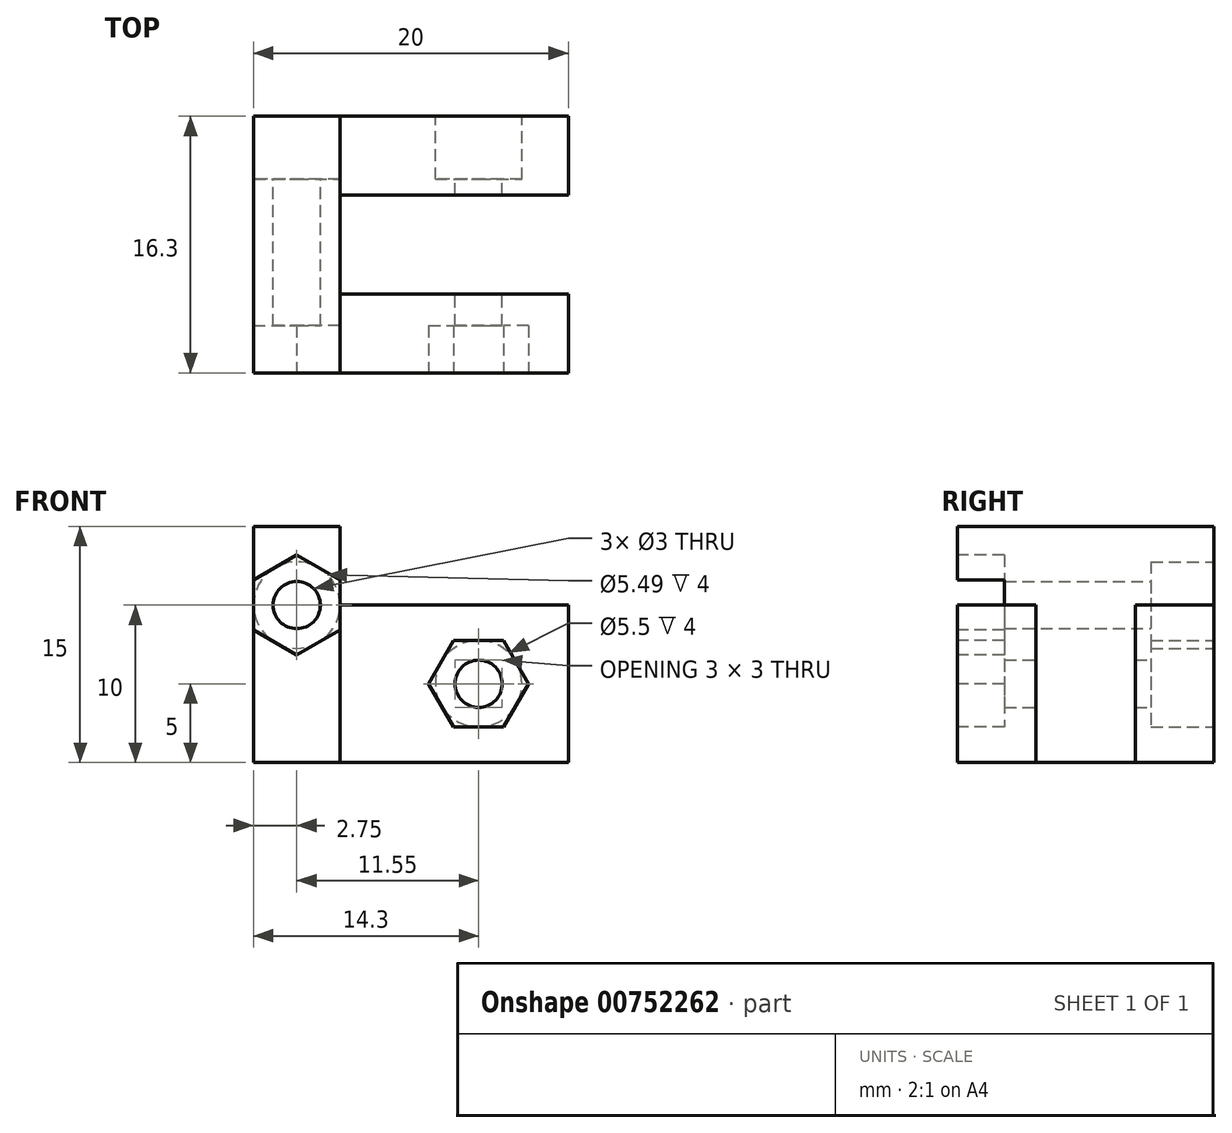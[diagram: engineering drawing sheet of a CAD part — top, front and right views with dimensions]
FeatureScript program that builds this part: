
annotation { "Feature Type Name" : "Feature", "Feature Type Description" : "" }
export const myFeature = defineFeature(function(context is Context, id is Id, definition is map)
    precondition{}
    {
        {
            var Q0;
            Q0=qCreatedBy(makeId("Top.planeOp"),FACE);
            var sketch = newSketch(context, id + "F0", { "sketchPlane" : qUnion([Q0])});
            skLineSegment(sketch, "E0", {"start": v(0, -3.15) * mm, "end": v(-14.5, -3.15) * mm});
            skLineSegment(sketch, "E1", {"start": v(0, -3.15) * mm, "end": v(0, -8.15) * mm});
            skLineSegment(sketch, "E2", {"start": v(0, -8.15) * mm, "end": v(-14.5, -8.15) * mm});
            skLineSegment(sketch, "E3", {"start": v(-14.5, -8.15) * mm, "end": v(-20, -8.15) * mm});
            skLineSegment(sketch, "E4", {"start": v(-20, -8.15) * mm, "end": v(-20, 0) * mm});
            skLineSegment(sketch, "E5", {"start": v(-14.5, -3.15) * mm, "end": v(-14.5, 0) * mm});
            skLineSegment(sketch, "E6.MirrorCS", {"start": v(-14.5, 8.15) * mm, "end": v(-20, 8.15) * mm});
            skLineSegment(sketch, "E7.MirrorCS", {"start": v(0, 8.15) * mm, "end": v(-14.5, 8.15) * mm});
            skLineSegment(sketch, "E8.MirrorCS", {"start": v(-20, 8.15) * mm, "end": v(-20, 0) * mm});
            skLineSegment(sketch, "E9.MirrorCS", {"start": v(0, 3.15) * mm, "end": v(0, 8.15) * mm});
            skLineSegment(sketch, "E10.MirrorCS", {"start": v(-14.5, 3.15) * mm, "end": v(-14.5, 0) * mm});
            skLineSegment(sketch, "E11.MirrorCS", {"start": v(0, 3.15) * mm, "end": v(-14.5, 3.15) * mm});
            skLineSegment(sketch, "E12", {"start": v(-14.5, 3.15) * mm, "end": v(-14.5, 8.15) * mm});
            skLineSegment(sketch, "E13", {"start": v(-14.5, -3.15) * mm, "end": v(-14.5, -8.15) * mm});
            skSolve(sketch);
        }
        {
            var Q0;
            Q0=makeQuery(id+"F0.imprint","IMPRINT",FACE,{"disambiguationData":[TD([[makeQuery(id+"F0.imprint","IMPRINT",EDGE,{"derivedFrom":sQuery(id+"F0.wireOp",EDGE,"E7.MirrorCS")}),1.0]])]});
            var Q1;
            Q1=makeQuery(id+"F0.imprint","IMPRINT",FACE,{"disambiguationData":[TD([[makeQuery(id+"F0.imprint","IMPRINT",EDGE,{"derivedFrom":sQuery(id+"F0.wireOp",EDGE,"E0")}),1.0]])]});
            extrude(context, id + "F1", {"entities" : qUnion([Q0, Q1]), "depth" : 10 * mm, "offsetDistance" : 25 * mm});
        }
        {
            var Q0;
            Q0=makeQuery(id+"F0.imprint","IMPRINT",FACE,{"disambiguationData":[TD([[makeQuery(id+"F0.imprint","IMPRINT",EDGE,{"derivedFrom":sQuery(id+"F0.wireOp",EDGE,"E3")}),-1.0]])]});
            extrude(context, id + "F2", {"entities" : qUnion([Q0]), "depth" : 15 * mm, "offsetDistance" : 25 * mm});
        }
        {
            var Q0;
            Q0=makeQuery(id+"F1.opExtrude","SWEPT_FACE",FACE,{"disambiguationData":[OSD([sQuery(id+"F0.wireOp",EDGE,"E7.MirrorCS")])]});
            var sketch = newSketch(context, id + "F3", { "sketchPlane" : qUnion([Q0])});
            skPoint(sketch, "E14", {"position": v(17.25, 10) * mm});
            skCircle(sketch, "E15", {"center": v(17.25, 10) * mm, "radius": 1.5 * mm});
            skCircle(sketch, "E16", {"center": v(17.25, 10) * mm, "radius": 2.75 * mm});
            skPoint(sketch, "E17", {"position": v(5.7, 5) * mm});
            skCircle(sketch, "E18", {"center": v(5.7, 5) * mm, "radius": 1.5 * mm});
            skCircle(sketch, "E19", {"center": v(5.7, 5) * mm, "radius": 2.75 * mm});
            skSolve(sketch);
        }
        {
            var Q0;
            Q0=makeQuery(id+"F3.imprint","IMPRINT",FACE,{"disambiguationData":[TD([[makeQuery(id+"F3.imprint","IMPRINT",EDGE,{"derivedFrom":sQuery(id+"F3.wireOp",EDGE,"E18")}),1.0]])]});
            var Q1;
            Q1=makeQuery(id+"F3.imprint","IMPRINT",FACE,{"disambiguationData":[TD([[makeQuery(id+"F3.imprint","IMPRINT",EDGE,{"derivedFrom":sQuery(id+"F3.wireOp",EDGE,"E15")}),1.0]])]});
            extrude(context, id + "F4", {"entities" : qUnion([Q0, Q1]), "operationType" : NewBodyOperationType.REMOVE, "oppositeDirection" : true, "depth" : 16.3 * mm, "offsetDistance" : 25 * mm});
        }
        {
            var Q0;
            Q0=makeQuery(id+"F3.imprint","IMPRINT",FACE,{"disambiguationData":[TD([[makeQuery(id+"F3.imprint","IMPRINT",EDGE,{"derivedFrom":sQuery(id+"F3.wireOp",EDGE,"E15")}),-1.0]])]});
            var Q1;
            Q1=makeQuery(id+"F3.imprint","IMPRINT",FACE,{"disambiguationData":[TD([[makeQuery(id+"F3.imprint","IMPRINT",EDGE,{"derivedFrom":sQuery(id+"F3.wireOp",EDGE,"E18")}),-1.0]])]});
            extrude(context, id + "F5", {"entities" : qUnion([Q0, Q1]), "operationType" : NewBodyOperationType.REMOVE, "oppositeDirection" : true, "depth" : 4 * mm, "offsetDistance" : 25 * mm});
        }
        {
            var Q0;
            Q0=makeQuery(id+"F1.opExtrude","SWEPT_FACE",FACE,{"disambiguationData":[OSD([sQuery(id+"F0.wireOp",EDGE,"E2")])]});
            var sketch = newSketch(context, id + "F6", { "sketchPlane" : qUnion([Q0])});
            skCircle(sketch, "E20.cCircle", {"center": v(-5.7, 5) * mm, "radius": 3.18 * mm, "construction": true});
            skPoint(sketch, "E20.cCircle.perimeterSnap0", {"position": v(0, 5) * mm});
            skLineSegment(sketch, "E20.0", {"start": v(-2.52, 5) * mm, "end": v(-4.11, 2.25) * mm});
            skPoint(sketch, "E20.0.startSnap0", {"position": v(0, 5) * mm});
            skLineSegment(sketch, "E20.1", {"start": v(-4.11, 2.25) * mm, "end": v(-7.29, 2.25) * mm});
            skLineSegment(sketch, "E20.2", {"start": v(-7.29, 2.25) * mm, "end": v(-8.88, 5) * mm});
            skLineSegment(sketch, "E20.3", {"start": v(-8.88, 5) * mm, "end": v(-7.29, 7.75) * mm});
            skLineSegment(sketch, "E20.4", {"start": v(-7.29, 7.75) * mm, "end": v(-4.11, 7.75) * mm});
            skLineSegment(sketch, "E20.5", {"start": v(-4.11, 7.75) * mm, "end": v(-2.52, 5) * mm});
            skSolve(sketch);
        }
        {
            var Q0;
            Q0=makeQuery(id+"F6.imprint","IMPRINT",FACE,{"disambiguationData":[TD([[makeQuery(id+"F6.imprint","IMPRINT",EDGE,{"derivedFrom":sQuery(id+"F6.wireOp",EDGE,"E20.0")}),-1.0]])]});
            extrude(context, id + "F7", {"entities" : qUnion([Q0]), "operationType" : NewBodyOperationType.REMOVE, "oppositeDirection" : true, "depth" : 3 * mm, "offsetDistance" : 25 * mm});
        }
        {
            var Q0;
            Q0=makeQuery(id+"F2.opExtrude","SWEPT_FACE",FACE,{"disambiguationData":[OSD([sQuery(id+"F0.wireOp",EDGE,"E3")])]});
            var sketch = newSketch(context, id + "F8", { "sketchPlane" : qUnion([Q0])});
            skCircle(sketch, "E21.cCircle", {"center": v(-17.25, 10) * mm, "radius": 3.18 * mm, "construction": true});
            skPoint(sketch, "E21.cCircle.perimeterSnap0", {"position": v(-17.25, 15) * mm});
            skLineSegment(sketch, "E21.0", {"start": v(-17.25, 13.18) * mm, "end": v(-14.5, 11.59) * mm});
            skPoint(sketch, "E21.0.startSnap0", {"position": v(-17.25, 15) * mm});
            skLineSegment(sketch, "E21.1", {"start": v(-14.5, 11.59) * mm, "end": v(-14.5, 8.41) * mm});
            skLineSegment(sketch, "E21.2", {"start": v(-14.5, 8.41) * mm, "end": v(-17.25, 6.82) * mm});
            skLineSegment(sketch, "E21.3", {"start": v(-17.25, 6.82) * mm, "end": v(-20, 8.41) * mm});
            skLineSegment(sketch, "E21.4", {"start": v(-20, 8.41) * mm, "end": v(-20, 11.59) * mm});
            skLineSegment(sketch, "E21.5", {"start": v(-20, 11.59) * mm, "end": v(-17.25, 13.18) * mm});
            skSolve(sketch);
        }
        {
            var Q0;
            Q0=makeQuery(id+"F8.imprint","IMPRINT",FACE,{"disambiguationData":[TD([[makeQuery(id+"F8.imprint","IMPRINT",EDGE,{"derivedFrom":sQuery(id+"F8.wireOp",EDGE,"E21.0")}),-1.0]])]});
            extrude(context, id + "F9", {"entities" : qUnion([Q0]), "operationType" : NewBodyOperationType.REMOVE, "oppositeDirection" : true, "depth" : 3 * mm, "offsetDistance" : 25 * mm});
        }
    });
